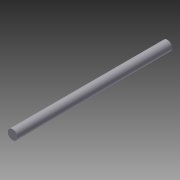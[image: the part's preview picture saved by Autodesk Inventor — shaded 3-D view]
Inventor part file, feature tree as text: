
AUTODESK INVENTOR PART (.ipt)
format: ipt  version: 2011 (Build 150239000, 239)  size: 60,416 bytes
history: native  units: in
note: dims shown in document units (in); Inventor stores cm internally (conversion verified against a paired STEP export)
features: extrude x1, sketch x1
ambient origin geometry x8: Origin, YZ Plane, XZ Plane, XY Plane, X Axis, Y Axis, Z Axis, Center Point
bodies: Solid1 (feature_tree)
feature tree (2):
  extrude  "Extrusion1"  Depth=12.0in TaperAngle=0.0deg
  sketch  "Sketch1"  dims[d0=0.75in d1=12.0in d2=0.0in]
